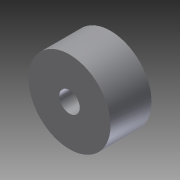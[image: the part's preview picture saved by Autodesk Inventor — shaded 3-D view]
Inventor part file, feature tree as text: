
AUTODESK INVENTOR PART (.ipt)
format: ipt  version: 2011 (Build 150239000, 239)  size: 75,264 bytes
history: native  units: in
note: dims shown in document units (in); Inventor stores cm internally (conversion verified against a paired STEP export)
features: extrude x1, sketch x1
ambient origin geometry x8: Origin, YZ Plane, XZ Plane, XY Plane, X Axis, Y Axis, Z Axis, Center Point
bodies: Solid1 (feature_tree)
feature tree (2):
  extrude  "Extrusion1"  Depth=0.125in
  sketch  "Sketch1"  dims[d1=0.5in d2=0.125in d3=0.25in d4=0.0in]
